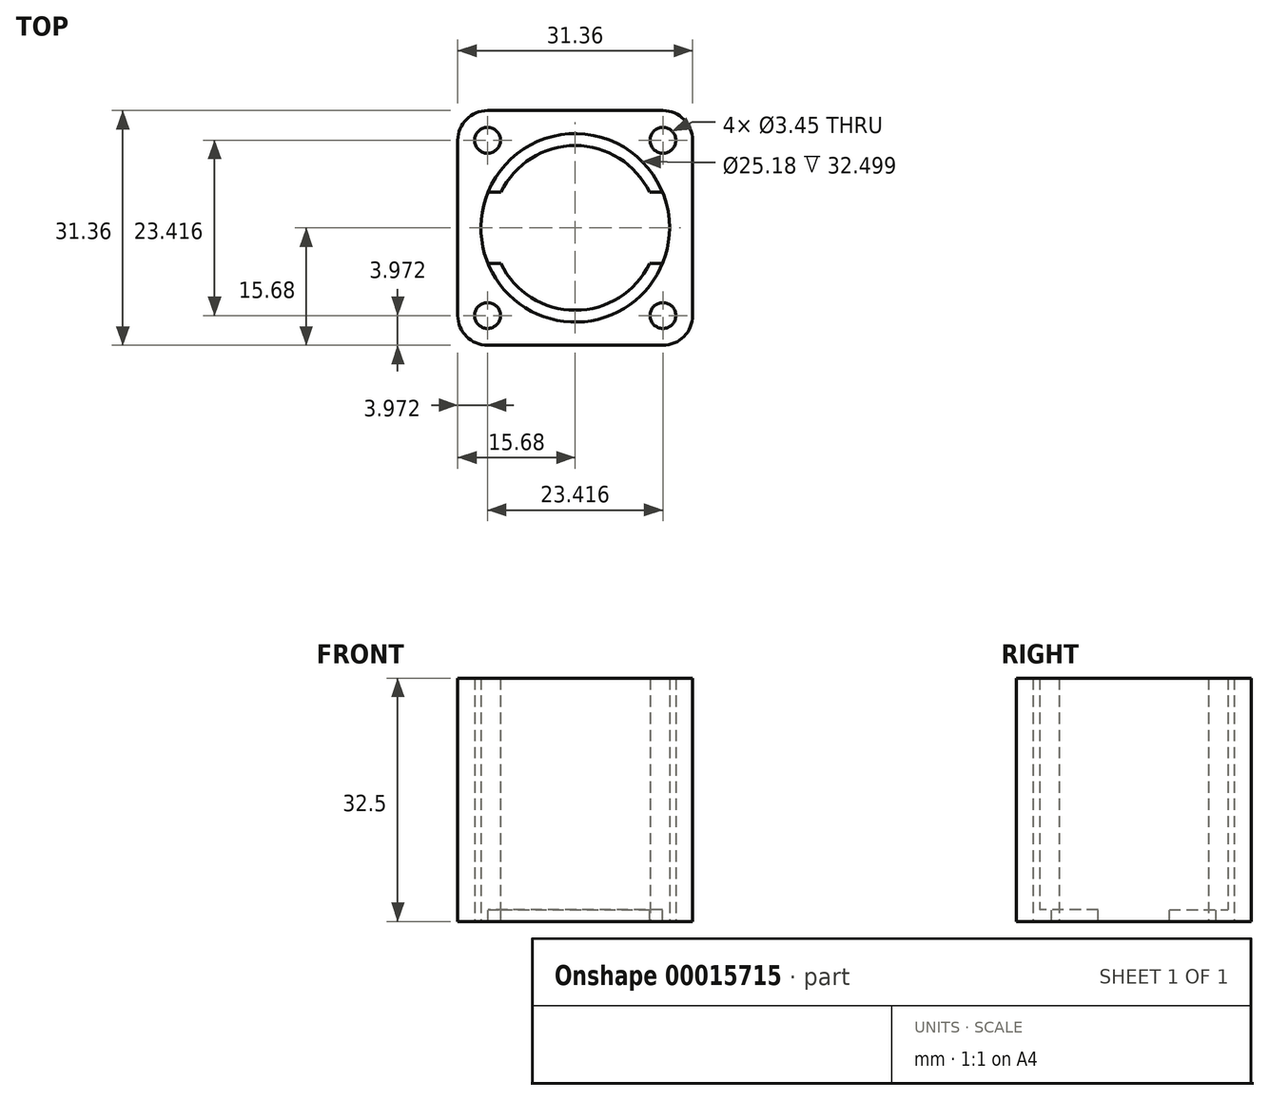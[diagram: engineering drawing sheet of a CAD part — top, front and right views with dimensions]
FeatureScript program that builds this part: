
annotation { "Feature Type Name" : "Feature", "Feature Type Description" : "" }
export const myFeature = defineFeature(function(context is Context, id is Id, definition is map)
    precondition{}
    {
        {
            var Q0;
            Q0=qCreatedBy(makeId("Top.planeOp"),FACE);
            var sketch = newSketch(context, id + "F0", { "sketchPlane" : qUnion([Q0])});
            skCircle(sketch, "E0", {"center": v(0, 0) * mm, "radius": 12.59 * mm});
            skLineSegment(sketch, "E1.rect.bottom", {"start": v(15.68, -15.68) * mm, "end": v(-15.68, -15.68) * mm});
            skLineSegment(sketch, "E1.rect.top", {"start": v(15.68, 15.68) * mm, "end": v(-15.68, 15.68) * mm});
            skLineSegment(sketch, "E1.rect.left", {"start": v(15.68, -15.68) * mm, "end": v(15.68, 15.68) * mm});
            skLineSegment(sketch, "E1.rect.right", {"start": v(-15.68, -15.68) * mm, "end": v(-15.68, 15.68) * mm});
            skCircle(sketch, "E2", {"center": v(11.7, -11.7) * mm, "radius": 3.97 * mm, "construction": true});
            skCircle(sketch, "E3", {"center": v(11.7, -11.7) * mm, "radius": 1.73 * mm});
            skCircle(sketch, "E4", {"center": v(11.7, 11.7) * mm, "radius": 3.97 * mm, "construction": true});
            skCircle(sketch, "E5", {"center": v(11.7, 11.7) * mm, "radius": 1.73 * mm});
            skCircle(sketch, "E6", {"center": v(-11.7, 11.7) * mm, "radius": 3.97 * mm, "construction": true});
            skCircle(sketch, "E7", {"center": v(-11.7, 11.7) * mm, "radius": 1.73 * mm});
            skCircle(sketch, "E8", {"center": v(-11.7, -11.7) * mm, "radius": 3.97 * mm, "construction": true});
            skCircle(sketch, "E9", {"center": v(-11.7, -11.7) * mm, "radius": 1.73 * mm});
            skSolve(sketch);
        }
        {
            var Q0;
            Q0=qSketchRegion(id+"F0",true);
            extrude(context, id + "F1", {"entities" : qUnion([Q0]), "depth" : 30.91 * mm});
        }
        {
            var Q0;
            Q0=makeQuery(id+"F1.opExtrude","CAP_FACE",FACE,{"disambiguationData":[OSD([sQuery(id+"F0.wireOp",EDGE,"E0"),sQuery(id+"F0.wireOp",EDGE,"E1.rect.bottom"),sQuery(id+"F0.wireOp",EDGE,"E1.rect.top"),sQuery(id+"F0.wireOp",EDGE,"E1.rect.left"),sQuery(id+"F0.wireOp",EDGE,"E1.rect.right"),sQuery(id+"F0.wireOp",EDGE,"E3"),sQuery(id+"F0.wireOp",EDGE,"E5"),sQuery(id+"F0.wireOp",EDGE,"E7"),sQuery(id+"F0.wireOp",EDGE,"E9")])],"isStart":true});
            var sketch = newSketch(context, id + "F2", { "sketchPlane" : qUnion([Q0])});
            skLineSegment(sketch, "E10.rect.bottom", {"start": v(15.68, 15.68) * mm, "end": v(-15.68, 15.68) * mm});
            skLineSegment(sketch, "E10.rect.top", {"start": v(15.68, -15.68) * mm, "end": v(-15.68, -15.68) * mm});
            skLineSegment(sketch, "E10.rect.left", {"start": v(15.68, 15.68) * mm, "end": v(15.68, -15.68) * mm});
            skLineSegment(sketch, "E10.rect.right", {"start": v(-15.68, 15.68) * mm, "end": v(-15.68, -15.68) * mm});
            skPoint(sketch, "E10.rect.middle", {"position": v(0, 0) * mm});
            skCircle(sketch, "E11", {"center": v(0, 0) * mm, "radius": 11 * mm});
            skSolve(sketch);
        }
        {
            var Q0;
            Q0=makeQuery(id+"F2.imprint","IMPRINT",FACE,{"disambiguationData":[TD([[makeQuery(id+"F2.imprint","IMPRINT",EDGE,{"derivedFrom":sQuery(id+"F2.wireOp",EDGE,"E11")}),-1.0]])]});
            var Q1;
            Q1=makeQuery(id+"F2.imprint","IMPRINT",FACE,{"disambiguationData":[TD([[makeQuery(id+"F2.imprint","IMPRINT",EDGE,{"derivedFrom":sQuery(id+"F2.wireOp",EDGE,"E10.rect.bottom")}),1.0]])]});
            extrude(context, id + "F3", {"entities" : qUnion([Q0, Q1]), "operationType" : NewBodyOperationType.ADD, "depth" : 1.59 * mm});
        }
        {
            var Q0;
            Q0=makeQuery(id+"F3.boolean.opBoolean","MERGE",EDGE,{"derivedFrom":[makeQuery(id+"F1.opExtrude","SWEPT_EDGE",EDGE,{"disambiguationData":[OSD([sQuery(id+"F0.wireOp",EDGE,"E1.rect.top"),sQuery(id+"F0.wireOp",EDGE,"E1.rect.right")])]}),makeQuery(id+"F3.opExtrude","SWEPT_EDGE",EDGE,{"disambiguationData":[OSD([sQuery(id+"F2.wireOp",EDGE,"E10.rect.top"),sQuery(id+"F2.wireOp",EDGE,"E10.rect.right")])]})]});
            var Q1;
            Q1=makeQuery(id+"F3.boolean.opBoolean","MERGE",EDGE,{"derivedFrom":[makeQuery(id+"F1.opExtrude","SWEPT_EDGE",EDGE,{"disambiguationData":[OSD([sQuery(id+"F0.wireOp",EDGE,"E1.rect.top"),sQuery(id+"F0.wireOp",EDGE,"E1.rect.left")])]}),makeQuery(id+"F3.opExtrude","SWEPT_EDGE",EDGE,{"disambiguationData":[OSD([sQuery(id+"F2.wireOp",EDGE,"E10.rect.top"),sQuery(id+"F2.wireOp",EDGE,"E10.rect.left")])]})]});
            var Q2;
            Q2=makeQuery(id+"F3.boolean.opBoolean","MERGE",EDGE,{"derivedFrom":[makeQuery(id+"F1.opExtrude","SWEPT_EDGE",EDGE,{"disambiguationData":[OSD([sQuery(id+"F0.wireOp",EDGE,"E1.rect.bottom"),sQuery(id+"F0.wireOp",EDGE,"E1.rect.left")])]}),makeQuery(id+"F3.opExtrude","SWEPT_EDGE",EDGE,{"disambiguationData":[OSD([sQuery(id+"F2.wireOp",EDGE,"E10.rect.bottom"),sQuery(id+"F2.wireOp",EDGE,"E10.rect.left")])]})]});
            var Q3;
            Q3=makeQuery(id+"F3.boolean.opBoolean","MERGE",EDGE,{"derivedFrom":[makeQuery(id+"F1.opExtrude","SWEPT_EDGE",EDGE,{"disambiguationData":[OSD([sQuery(id+"F0.wireOp",EDGE,"E1.rect.bottom"),sQuery(id+"F0.wireOp",EDGE,"E1.rect.right")])]}),makeQuery(id+"F3.opExtrude","SWEPT_EDGE",EDGE,{"disambiguationData":[OSD([sQuery(id+"F2.wireOp",EDGE,"E10.rect.bottom"),sQuery(id+"F2.wireOp",EDGE,"E10.rect.right")])]})]});
            fillet(context, id + "F4", {"entities" : qUnion([Q0, Q1, Q2, Q3]), "radius" : 3.97 * mm, "tangentPropagation" : true, "allowEdgeOverflow" : false});
        }
        {
            var Q0;
            Q0=makeQuery(id+"F3.opExtrude","CAP_FACE",FACE,{"disambiguationData":[OSD([sQuery(id+"F0.wireOp",EDGE,"E3"),sQuery(id+"F0.wireOp",EDGE,"E5"),sQuery(id+"F0.wireOp",EDGE,"E7"),sQuery(id+"F0.wireOp",EDGE,"E9"),sQuery(id+"F2.wireOp",EDGE,"E10.rect.bottom"),sQuery(id+"F2.wireOp",EDGE,"E10.rect.top"),sQuery(id+"F2.wireOp",EDGE,"E10.rect.left"),sQuery(id+"F2.wireOp",EDGE,"E10.rect.right"),sQuery(id+"F2.wireOp",EDGE,"E11")])],"isStart":true});
            var sketch = newSketch(context, id + "F5", { "sketchPlane" : qUnion([Q0])});
            skArc(sketch, "E12", {"start": v(-9.92, 4.76) * mm, "mid": v(-11, 0) * mm, "end": v(-9.92, -4.76) * mm});
            skArc(sketch, "E13", {"start": v(-11.65, 4.76) * mm, "mid": v(-12.59, 0) * mm, "end": v(-11.65, -4.76) * mm});
            skArc(sketch, "E14", {"start": v(9.92, -4.76) * mm, "mid": v(11, 0) * mm, "end": v(9.92, 4.76) * mm});
            skArc(sketch, "E15", {"start": v(11.65, -4.76) * mm, "mid": v(12.59, 0) * mm, "end": v(11.65, 4.76) * mm});
            skLineSegment(sketch, "E16", {"start": v(-11.65, -4.76) * mm, "end": v(-9.92, -4.76) * mm});
            skLineSegment(sketch, "E17", {"start": v(-11.65, 4.76) * mm, "end": v(-9.92, 4.76) * mm});
            skLineSegment(sketch, "E18", {"start": v(11.65, 4.76) * mm, "end": v(9.92, 4.76) * mm});
            skLineSegment(sketch, "E19", {"start": v(9.92, -4.76) * mm, "end": v(11.65, -4.76) * mm});
            skLineSegment(sketch, "E20", {"start": v(-11, 0) * mm, "end": v(11, 0) * mm});
            skSolve(sketch);
        }
        {
            var Q0;
            Q0=qSketchRegion(id+"F5",true);
            extrude(context, id + "F6", {"entities" : qUnion([Q0]), "operationType" : NewBodyOperationType.REMOVE, "oppositeDirection" : true, "depth" : 25.4 * mm});
        }
    });
